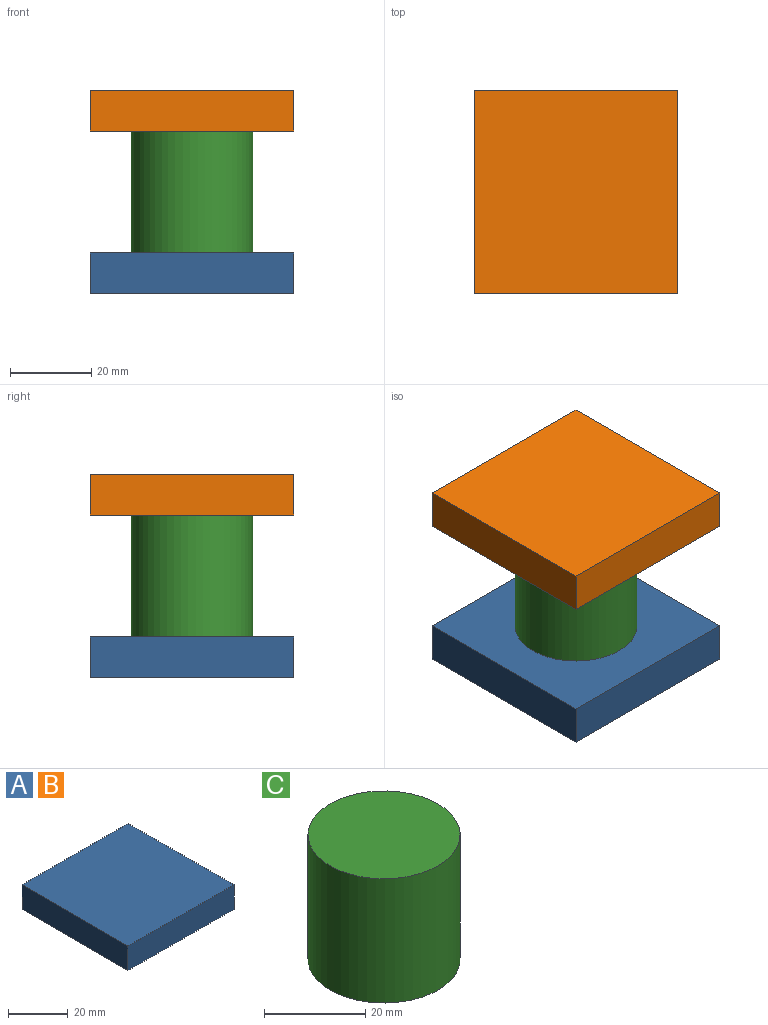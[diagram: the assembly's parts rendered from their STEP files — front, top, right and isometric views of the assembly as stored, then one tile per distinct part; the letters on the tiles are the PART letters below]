
ASSEMBLY  parts=3 mates=2
PART A: 6 faces, bbox 50x50x10 mm
  f0: plane 50x10mm, normal (0,-1,0), area 500mm2, adj f1,f3,f4,f5
  f1: plane 50x10mm, normal (1,0,0), area 500mm2, adj f0,f2,f4,f5
  f2: plane 50x10mm, normal (0,1,0), area 500mm2, adj f1,f3,f4,f5
  f3: plane 50x10mm, normal (-1,0,0), area 500mm2, adj f0,f2,f4,f5
  f4: plane 50x50mm, normal (0,0,1), area 2500mm2, adj f0,f1,f2,f3
  f5: plane 50x50mm, normal (0,0,-1), area 2500mm2, adj f0,f1,f2,f3
PART B: same geometry as A
PART C: 3 faces, bbox 30x30x30 mm
  f0: cylinder r=15mm len=30mm, axis (0,0,-1), area 2827.4mm2, adj f1,f2
  f1: plane 30x30mm, normal (0,0,1), area 706.9mm2, adj f0
  f2: plane 30x30mm, normal (0,0,-1), area 706.9mm2, adj f0
PLACE A t=(29,5.02,-62.58)mm
PLACE B t=(29,5.02,-22.58)mm
PLACE C t=(29,5.02,-52.58)mm
MATE fastened A.f4 <-> C.f0  axis (0,0,1) through (29,5.02,-52.58)mm
MATE fastened C.f0 <-> B.f5  axis (0,0,1) through (29,5.02,-22.58)mm
